# Revit family: Flowerpot pendant VP1
name_source: partatom
category: Generic Models
revit_build: Autodesk Revit 2017 (Build: 20171027_0315(x64)
units: mm (PartAtom-declared; Revit-internal decimal feet)

## family parameters
Always vertical = Yes
Can host rebar = No
Cut with Voids When Loaded = No
Host = Ceiling
Part Type = Normal
Room Calculation Point = No
Round Connector Dimension = Use Diameter
Shared = Yes

## types (1)
- VP1
    Canopy = &tradition Plastic White Matt
    Cord = &tradition Textile cord - Stone Blue (NCS S 6005-B80G)
    Description = The Flowerpot lamp became synonymous with the Flower Power movement from the late 60s. Reflecting a break from convention to embrace a more open, modern mentality that promoted peace and harmony. Such was the mindset of its designer, Verner Panton. One of the most forward-thinking talents of his time. The Flowerpot series consitsts of several different models, including three pendants and two table lamps - all in a wide range of colours.
    Design = Verner Panton
    Design Year = 1968
    Diameter = 23cm / 9.1in
    Height = 16cm / 6.3
    Lamp Shade bearing = &tradition Plastic White Matt
    Lamp shade = &tradition Laquered metal - Stone Blue (NCS S 6005-B80G)
    Lamp shade inside = &tradition Powder Coated Aluminium white
    Lamp top = &tradition Chrome
    Manufacturer = &Tradition
    Model = Flowerpot VP1
    Packaging Dimensions = H15.0cm/5.9in, W24.5cm/9.6in, D25.0cm/9.8in
    Socket = &tradition White porcelain
    Type Comments = Flowerpot series
    URL = https://www.andtradition.com
    Variations = Beige Red, Light Blue, Mustard, Red Brown, Grey Beige, Dark Green, White, Polished Brass, Polished Stainless Steel, Polished Copper, Matt Black, Matt Light Grey, Matt White
    Weight = 0.95kg

## geometry (parser evidence)
native form markers: Sweep x6
no freeform markers — native parametric forms only
